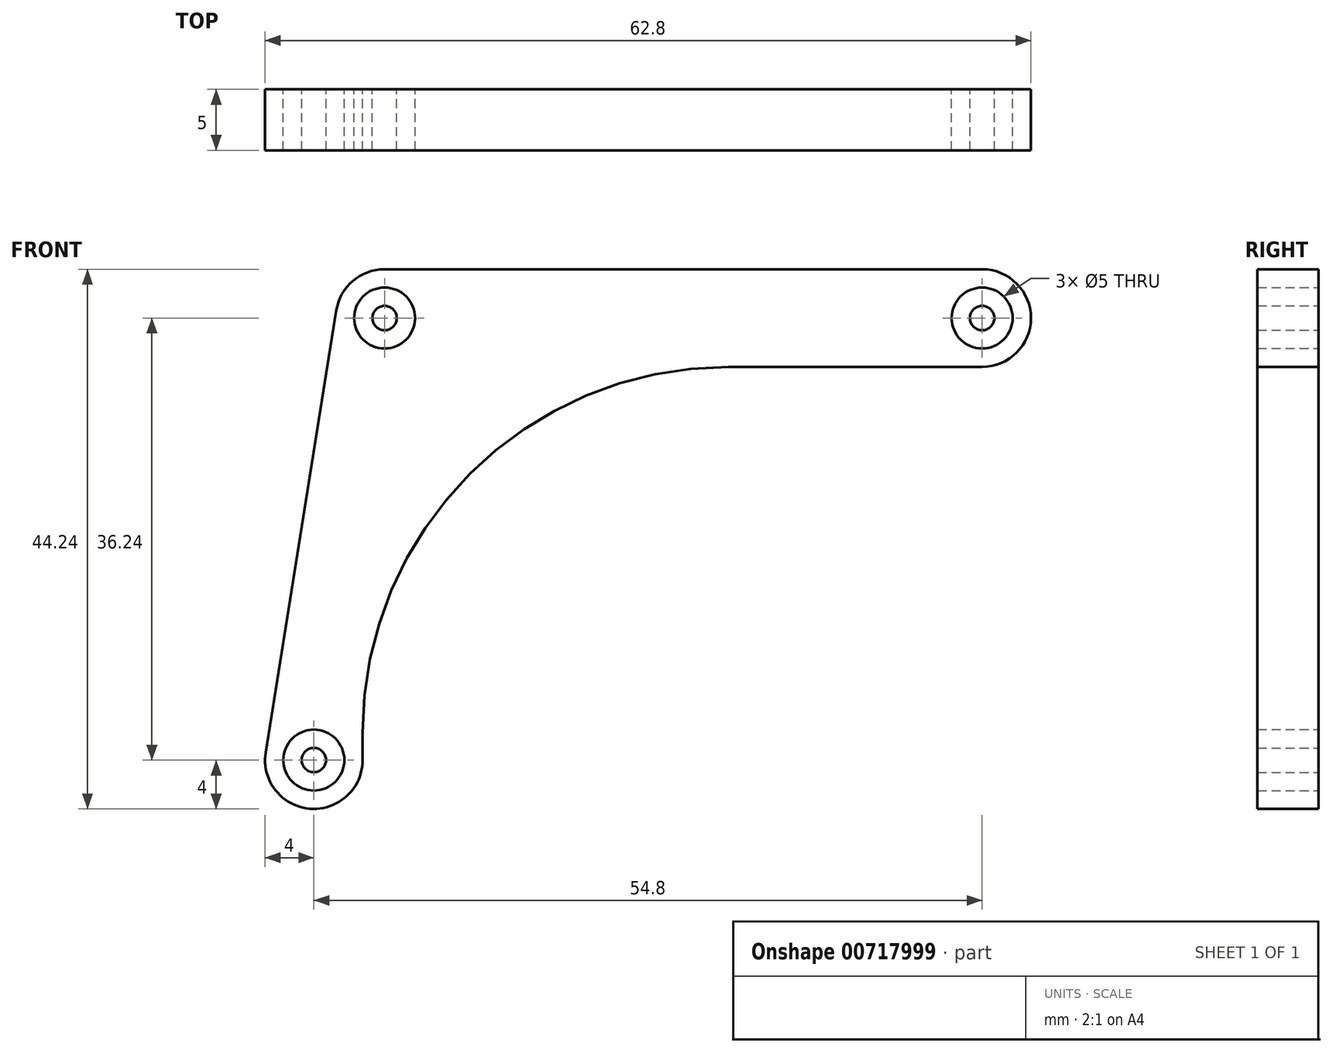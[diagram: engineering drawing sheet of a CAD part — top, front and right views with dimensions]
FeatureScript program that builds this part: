
annotation { "Feature Type Name" : "Feature", "Feature Type Description" : "" }
export const myFeature = defineFeature(function(context is Context, id is Id, definition is map)
    precondition{}
    {
        {
            var Q0;
            Q0=qCreatedBy(makeId("Front.planeOp"),FACE);
            var sketch = newSketch(context, id + "F0", { "sketchPlane" : qUnion([Q0])});
            skArc(sketch, "E0", {"start": v(0, 4) * mm, "mid": v(-2.6, 3.04) * mm, "end": v(-3.95, 0.63) * mm});
            skArc(sketch, "E1", {"start": v(49, -4) * mm, "mid": v(53, 0) * mm, "end": v(49, 4) * mm});
            skCircle(sketch, "E2", {"center": v(-5.8, -36.24) * mm, "radius": 4 * mm});
            skCircle(sketch, "E3", {"center": v(0, 0) * mm, "radius": 2.5 * mm});
            skCircle(sketch, "E4", {"center": v(49, 0) * mm, "radius": 2.5 * mm});
            skCircle(sketch, "E5", {"center": v(-5.8, -36.24) * mm, "radius": 2.5 * mm});
            skLineSegment(sketch, "E6", {"start": v(0, 4) * mm, "end": v(49, 4) * mm});
            skLineSegment(sketch, "E7", {"start": v(49, -4) * mm, "end": v(28.2, -4) * mm});
            skLineSegment(sketch, "E8", {"start": v(-1.8, -34) * mm, "end": v(-1.8, -36.24) * mm});
            skPoint(sketch, "E9.newPointA", {"position": v(0, -4) * mm});
            skPoint(sketch, "E9.newPointB", {"position": v(-1.8, 0) * mm});
            skArc(sketch, "E10", {"start": v(28.2, -4) * mm, "mid": v(6.99, -12.79) * mm, "end": v(-1.8, -34) * mm});
            skPoint(sketch, "E11.orphan", {"position": v(-1.8, -31.76) * mm});
            skLineSegment(sketch, "E12", {"start": v(-3.95, 0.63) * mm, "end": v(-9.75, -35.6) * mm});
            skCircle(sketch, "E13", {"center": v(0, 0) * mm, "radius": 1 * mm});
            skCircle(sketch, "E14", {"center": v(49, 0) * mm, "radius": 1 * mm});
            skCircle(sketch, "E15", {"center": v(-5.8, -36.24) * mm, "radius": 1 * mm});
            skSolve(sketch);
        }
        {
            var Q0;
            Q0 = qSketchRegion(id + "F0", true);
            var Q1;
            Q1=makeQuery(id+"F0.imprint","IMPRINT",FACE,{"disambiguationData":[TD([[makeQuery(id+"F0.imprint","IMPRINT",EDGE,{"derivedFrom":sQuery(id+"F0.wireOp",EDGE,"E15")}),1.0]])]});
            var Q2;
            Q2=makeQuery(id+"F0.imprint","IMPRINT",FACE,{"disambiguationData":[TD([[makeQuery(id+"F0.imprint","IMPRINT",EDGE,{"derivedFrom":sQuery(id+"F0.wireOp",EDGE,"E13")}),1.0]])]});
            var Q3;
            Q3=makeQuery(id+"F0.imprint","IMPRINT",FACE,{"disambiguationData":[TD([[makeQuery(id+"F0.imprint","IMPRINT",EDGE,{"derivedFrom":sQuery(id+"F0.wireOp",EDGE,"E14")}),1.0]])]});
            extrude(context, id + "F1", {"entities" : qUnion([Q0, Q1, Q2, Q3]), "depth" : 5 * mm, "offsetDistance" : 25 * mm});
        }
    });
